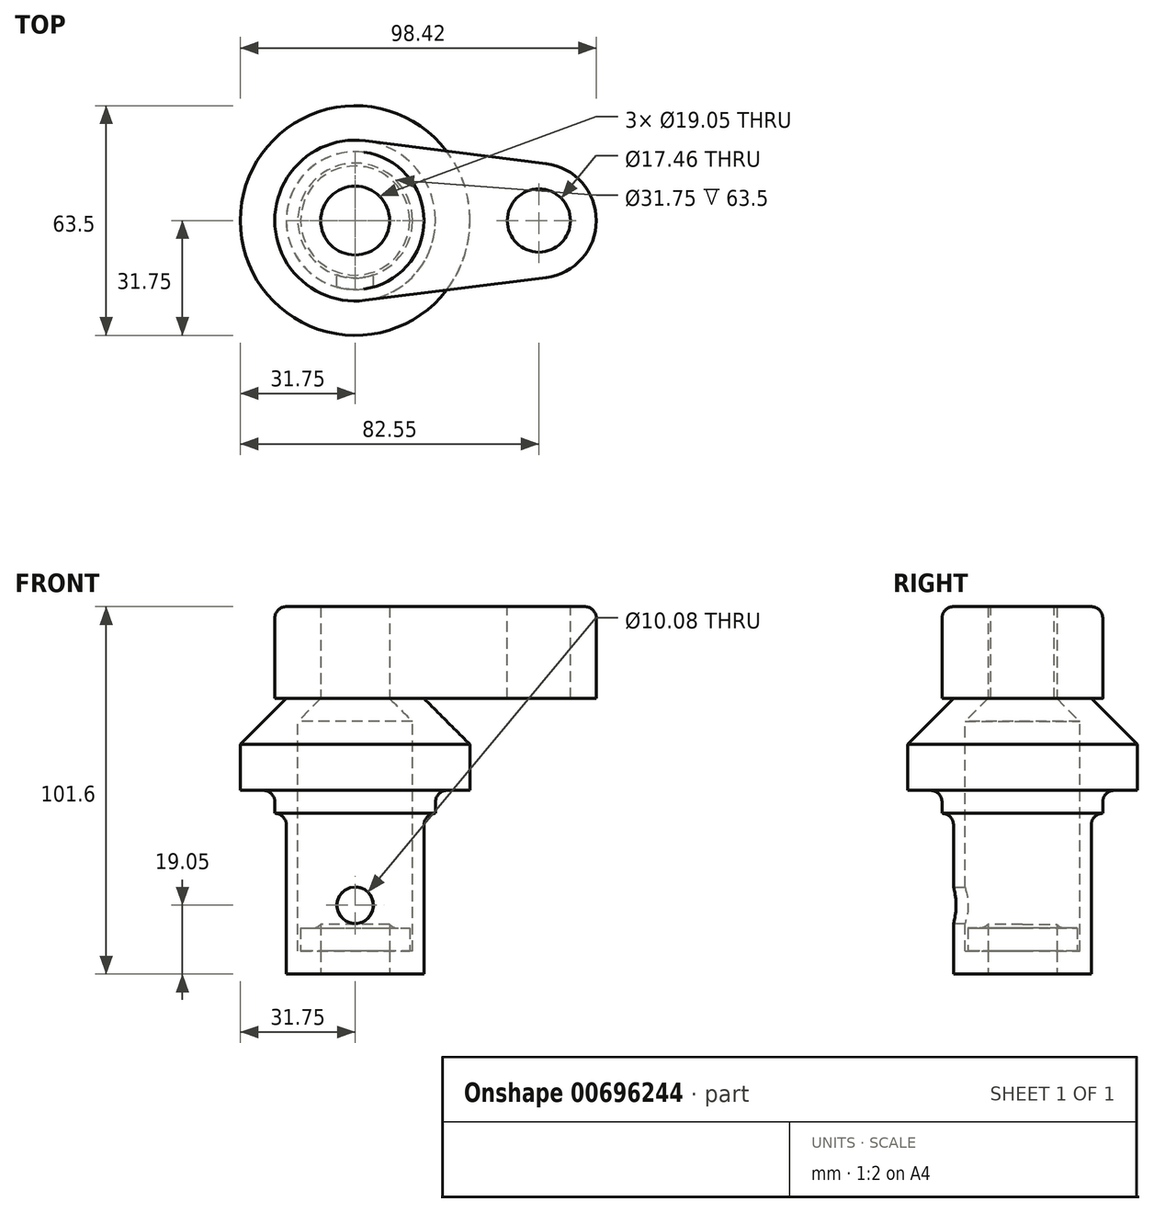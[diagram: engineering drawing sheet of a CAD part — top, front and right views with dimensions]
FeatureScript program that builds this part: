
annotation { "Feature Type Name" : "Feature", "Feature Type Description" : "" }
export const myFeature = defineFeature(function(context is Context, id is Id, definition is map)
    precondition{}
    {
        {
            var Q0;
            Q0=qCreatedBy(makeId("Front.planeOp"),FACE);
            var sketch = newSketch(context, id + "F0", { "sketchPlane" : qUnion([Q0])});
            skLineSegment(sketch, "E0", {"start": v(0, 0) * mm, "end": v(0, 76.2) * mm});
            skLineSegment(sketch, "E1", {"start": v(0, 76.2) * mm, "end": v(19.05, 76.2) * mm});
            skLineSegment(sketch, "E2", {"start": v(19.05, 76.2) * mm, "end": v(31.75, 63.5) * mm});
            skLineSegment(sketch, "E3", {"start": v(31.75, 63.5) * mm, "end": v(31.75, 50.8) * mm});
            skLineSegment(sketch, "E4", {"start": v(31.75, 50.8) * mm, "end": v(22.23, 50.8) * mm});
            skLineSegment(sketch, "E5", {"start": v(22.23, 50.8) * mm, "end": v(22.23, 44.45) * mm});
            skLineSegment(sketch, "E6", {"start": v(22.23, 44.45) * mm, "end": v(19.05, 44.45) * mm});
            skLineSegment(sketch, "E7", {"start": v(19.05, 44.45) * mm, "end": v(19.05, 0) * mm});
            skLineSegment(sketch, "E8", {"start": v(19.05, 0) * mm, "end": v(0, 0) * mm});
            skLineSegment(sketch, "E9", {"start": v(9.53, 76.2) * mm, "end": v(15.88, 69.85) * mm});
            skLineSegment(sketch, "E10", {"start": v(15.88, 69.85) * mm, "end": v(15.88, 6.35) * mm});
            skLineSegment(sketch, "E11", {"start": v(15.88, 6.35) * mm, "end": v(0, 6.35) * mm});
            skLineSegment(sketch, "E12", {"start": v(0, 76.2) * mm, "end": v(0, 91.75) * mm, "construction": true});
            skLineSegment(sketch, "E13", {"start": v(0, 76.2) * mm, "end": v(0, 101.6) * mm});
            skLineSegment(sketch, "E14", {"start": v(0, 101.6) * mm, "end": v(8.73, 101.6) * mm});
            skLineSegment(sketch, "E15", {"start": v(8.73, 101.6) * mm, "end": v(8.73, 12.7) * mm});
            skLineSegment(sketch, "E16", {"start": v(8.73, 12.7) * mm, "end": v(15.08, 12.7) * mm});
            skLineSegment(sketch, "E17", {"start": v(15.08, 12.7) * mm, "end": v(15.08, 6.35) * mm});
            skSolve(sketch);
        }
        {
            var Q0;
            {var subQ4=sQuery(id+"F0.wireOp",EDGE,"E2");Q0=makeQuery(id+"F0.imprint","IMPRINT",FACE,{"disambiguationData":[TD([[makeQuery(id+"F0.imprint","IMPRINT",EDGE,{"derivedFrom":subQ4}),-1.0]])]});}
            var Q1;
            Q1=sQuery(id+"F0.wireOp",EDGE,"E0");
            revolve(context, id + "F1", {"entities" : qUnion([Q0]), "axis" : qUnion([Q1]), "revolveType" : RevolveType.FULL, "oppositeDirection" : true});
        }
        {
            var Q0;
            {var subQ0=sQuery(id+"F0.wireOp",EDGE,"E13");Q0=makeQuery(id+"F0.imprint","IMPRINT",FACE,{"disambiguationData":[TD([[makeQuery(id+"F0.imprint","IMPRINT",EDGE,{"derivedFrom":subQ0}),-1.0]])]});}
            var Q1;
            {var subQ0=sQuery(id+"F0.wireOp",EDGE,"E16");Q1=makeQuery(id+"F0.imprint","IMPRINT",FACE,{"disambiguationData":[TD([[makeQuery(id+"F0.imprint","IMPRINT",EDGE,{"derivedFrom":subQ0}),-1.0]])]});}
            var Q2;
            Q2=sQuery(id+"F0.wireOp",EDGE,"E13");
            revolve(context, id + "F2", {"entities" : qUnion([Q0, Q1]), "axis" : qUnion([Q2]), "revolveType" : RevolveType.FULL});
        }
        {
            var Q0;
            Q0=makeQuery(id+"F2.opRevolve","SWEPT_FACE",FACE,{"disambiguationData":[OSD([sQuery(id+"F0.wireOp",EDGE,"E14")])]});
            var sketch = newSketch(context, id + "F3", { "sketchPlane" : qUnion([Q0])});
            skCircle(sketch, "E18", {"center": v(0, 0) * mm, "radius": 22.23 * mm});
            skCircle(sketch, "E19", {"center": v(50.8, 0) * mm, "radius": 15.88 * mm});
            skLineSegment(sketch, "E20", {"start": v(2.78, 22.05) * mm, "end": v(52.78, 15.75) * mm});
            skLineSegment(sketch, "E21", {"start": v(2.78, -22.05) * mm, "end": v(52.78, -15.75) * mm});
            skCircle(sketch, "E22.0", {"center": v(0, 0) * mm, "radius": 8.73 * mm});
            skCircle(sketch, "E23", {"center": v(50.8, 0) * mm, "radius": 8.73 * mm});
            skSolve(sketch);
        }
        {
            var Q0;
            Q0=makeQuery(id+"F3.imprint","IMPRINT",FACE,{"disambiguationData":[TD([[makeQuery(id+"F3.imprint","IMPRINT",EDGE,{"derivedFrom":sQuery(id+"F3.wireOp",EDGE,"E22.0")}),1.0]])]});
            var Q1;
            {var subQ0=sQuery(id+"F3.wireOp",EDGE,"E20");Q1=makeQuery(id+"F3.imprint","IMPRINT",FACE,{"disambiguationData":[TD([[makeQuery(id+"F3.imprint","IMPRINT",EDGE,{"derivedFrom":subQ0}),-1.0]])]});}
            var Q2;
            Q2=makeQuery(id+"F3.imprint","IMPRINT",FACE,{"disambiguationData":[TD([[makeQuery(id+"F3.imprint","IMPRINT",EDGE,{"derivedFrom":sQuery(id+"F3.wireOp",EDGE,"E23")}),-1.0]])]});
            var Q3;
            Q3=makeQuery(id+"F1.opRevolve","SWEPT_FACE",FACE,{"disambiguationData":[OSD([sQuery(id+"F0.wireOp",EDGE,"E1")])]});
            extrude(context, id + "F4", {"entities" : qUnion([Q0, Q1, Q2]), "oppositeDirection" : true, "depth" : 25.4 * mm, "endBoundEntityFace" : qUnion([Q3]), "offsetDistance" : 0.8 * mm});
        }
        {
            var Q0;
            Q0=qCreatedBy(makeId("Front.planeOp"),FACE);
            var sketch = newSketch(context, id + "F5", { "sketchPlane" : qUnion([Q0])});
            skPoint(sketch, "E24", {"position": v(0, 19.05) * mm});
            skSolve(sketch);
        }
        {
            var Q0;
            Q0=sQuery(id+"F5.wireOp",VERTEX,"E24");
            var Q1;
            Q1=makeQuery(id+"F1.opRevolve","SWEPT_BODY",BODY,{"disambiguationData":[OSD([sQuery(id+"F0.wireOp",EDGE,"E0"),sQuery(id+"F0.wireOp",EDGE,"E1"),sQuery(id+"F0.wireOp",EDGE,"E2"),sQuery(id+"F0.wireOp",EDGE,"E3"),sQuery(id+"F0.wireOp",EDGE,"E4"),sQuery(id+"F0.wireOp",EDGE,"E5"),sQuery(id+"F0.wireOp",EDGE,"E6"),sQuery(id+"F0.wireOp",EDGE,"E7"),sQuery(id+"F0.wireOp",EDGE,"E8"),sQuery(id+"F0.wireOp",EDGE,"E9"),sQuery(id+"F0.wireOp",EDGE,"E10"),sQuery(id+"F0.wireOp",EDGE,"E11")])]});
            hole(context, id + "F6", {"style" : HoleStyle.SIMPLE, "endStyle" : HoleEndStyle.THROUGH, "oppositeDirection" : true, "standardTappedOrClearance" : lookupTablePath({ "standard" : "ANSI", "fit" : "Normal (ASME)", "size" : "3/8", "type" : "Clearance" }), "standardBlindInLast" : lookupTablePath({ "fit" : "Free", "standard" : "ANSI", "size" : "3/8", "type" : "Clearance" }), "holeDiameter" : 10.08 * mm, "majorDiameter" : 6.35 * mm, "tappedDepth" : 14.3 * mm, "tapClearance" : 3, "locations" : qUnion([Q0]), "scope" : qUnion([Q1])});
        }
        {
            var Q0;
            Q0=makeQuery(id+"F4.opExtrude","CAP_EDGE",EDGE,{"disambiguationData":[OSD([sQuery(id+"F3.wireOp",EDGE,"E20")])],"isStart":true});
            var Q1;
            Q1=makeQuery(id+"F1.opRevolve","SWEPT_EDGE",EDGE,{"disambiguationData":[OSD([sQuery(id+"F0.wireOp",EDGE,"E4"),sQuery(id+"F0.wireOp",EDGE,"E5")])]});
            var Q2;
            Q2=makeQuery(id+"F1.opRevolve","SWEPT_EDGE",EDGE,{"disambiguationData":[OSD([sQuery(id+"F0.wireOp",EDGE,"E6"),sQuery(id+"F0.wireOp",EDGE,"E7")])]});
            var Q3;
            Q3=makeQuery(id+"F2.opRevolve","SWEPT_EDGE",EDGE,{"disambiguationData":[OSD([sQuery(id+"F0.wireOp",EDGE,"E15"),sQuery(id+"F0.wireOp",EDGE,"E16")])]});
            fillet(context, id + "F7", {"entities" : qUnion([Q0, Q1, Q2, Q3]), "radius" : 3.17 * mm, "tangentPropagation" : true, "allowEdgeOverflow" : false});
        }
        {
            var Q0;
            Q0=makeQuery(id+"F1.opRevolve","SWEPT_FACE",FACE,{"disambiguationData":[OSD([sQuery(id+"F0.wireOp",EDGE,"E8")])]});
            var sketch = newSketch(context, id + "F8", { "sketchPlane" : qUnion([Q0])});
            skCircle(sketch, "E25", {"center": v(0, 0) * mm, "radius": 9.53 * mm});
            skSolve(sketch);
        }
        {
            var Q0;
            Q0 = qSketchRegion(id + "F8", true);
            extrude(context, id + "F9", {"entities" : qUnion([Q0]), "operationType" : NewBodyOperationType.REMOVE, "endBound" : BoundingType.THROUGH_ALL, "oppositeDirection" : true, "depth" : 25.4 * mm, "offsetDistance" : 25.4 * mm});
        }
    });
